# Revit family: NLRS_C_31_WI_FB_VS41 dakrooster_jazo_jazo
name_source: partatom
category: Windows
units: mm (PartAtom-declared; Revit-internal decimal feet)

## family parameters
Cut with Voids When Loaded = Yes
Host = Face
OmniClass Number = 23.30.20.00
OmniClass Title = Windows
Room Calculation Point = No
Shared = No

## types (1)
- NLRS_C_31_WI_FB_VS41 dakrooster_jazo_jazo
    Assembly Code = 23.30.20.00
    Construction Type = Voor specificaties of mogelijkheden, neem contact op.
    Default Elevation = 0 mm  [stored 0 ft]
    Description = VS41 dakrooster
    Height = 1000 mm  [stored 3.28084 ft]
    JAZO_C_ca. totale netto doorlaat (cm2) = 2387.1 mm
    JAZO_C_materiaal profiel = <By Category>
    JAZO_C_materiaal schoep = <By Category>
    JAZO_C_opbouwrooster VS41 = Yes
    JAZO_C_vrije doorlaat breedte = 869 mm
    JAZO_C_vrije doorlaat hoogte = 670 mm  [stored 2.19816 ft]
    MAX HEIGHT = 2300 mm
    MAX WIDTH = 2926 mm  [stored 9.59974 ft]
    MIN HEIGHT = 500 mm  [stored 1.64042 ft]
    MIN WIDTH = 200 mm  [stored 0.656168 ft]
    Manufacturer = JAZO Zevenaar bv
    Model = VS41 dakrooster
    NLRS_C_aantal = 11
    NLRS_C_aantal_01 = 11
    NLRS_C_breedte = 1000 mm  [stored 3.28084 ft]
    NLRS_C_breedte_01 = 1010 mm  [stored 3.31365 ft]
    NLRS_C_breedte_02 = 984 mm  [stored 3.22835 ft]
    NLRS_C_breedte_max = 2926 mm  [stored 9.59974 ft]
    NLRS_C_breedte_min = 200 mm  [stored 0.656168 ft]
    NLRS_C_content_datum gewijzigd = 29-9-2022
    NLRS_C_content_datum uitgifte = 28-9-2022
    NLRS_C_content_provider = JAZO Zevenaar bv
    NLRS_C_content_revit versie = REVIT 2020.2
    NLRS_C_content_versie = 1.2
    NLRS_C_diepte = 88 mm  [stored 0.288714 ft]
    NLRS_C_geluidwering Rw = Voor specificaties of mogelijkheden, neem contact op.
    NLRS_C_hoogte = 1000 mm  [stored 3.28084 ft]
    NLRS_C_hoogte_01 = 1010 mm  [stored 3.31365 ft]
    NLRS_C_hoogte_max = 2300 mm
    NLRS_C_hoogte_min = 500 mm  [stored 1.64042 ft]
    NLRS_C_leverancier_adres = Handelsdwarsstraat 10
    NLRS_C_leverancier_bedrijfsnaam = JAZO Zevenaar bv
    NLRS_C_leverancier_plaats = Zevenaar
    NLRS_C_leverancier_postcode = 6905 DJ
    NLRS_C_leverancier_telefoonnummer = +31 316 - 59 29 11
    NLRS_C_leverancier_url = www.jazo.com
    NLRS_C_offset_01 = 8 mm  [stored 0.0262467 ft]
    NLRS_C_offset_02 = 32.5 mm  [stored 0.106627 ft]
    NLRS_C_offset_03 = 44.5 mm  [stored 0.145997 ft]
    NLRS_C_rookwerendheid = Voor specificaties of mogelijkheden, neem contact op.
    NLRS_C_stelruimte = 5 mm  [stored 0.0164042 ft]
    NLRS_C_weerstandsklasse = Voor specificaties of mogelijkheden, neem contact op.
    NLRS_C_zichtbaar_01 = No
    NLRS_C_zichtbaar_02 = Yes
    Rough Height = 1010 mm  [stored 3.31365 ft]
    Rough Width = 1010 mm  [stored 3.31365 ft]
    URL = www.jazo.com
    Width = 1000 mm  [stored 3.28084 ft]

note: [stored X ft] marks values corroborated as IEEE doubles in the binary element streams (Revit-internal decimal feet)

## geometry (parser evidence)
native form markers: Sweep x11
no freeform markers — native parametric forms only
